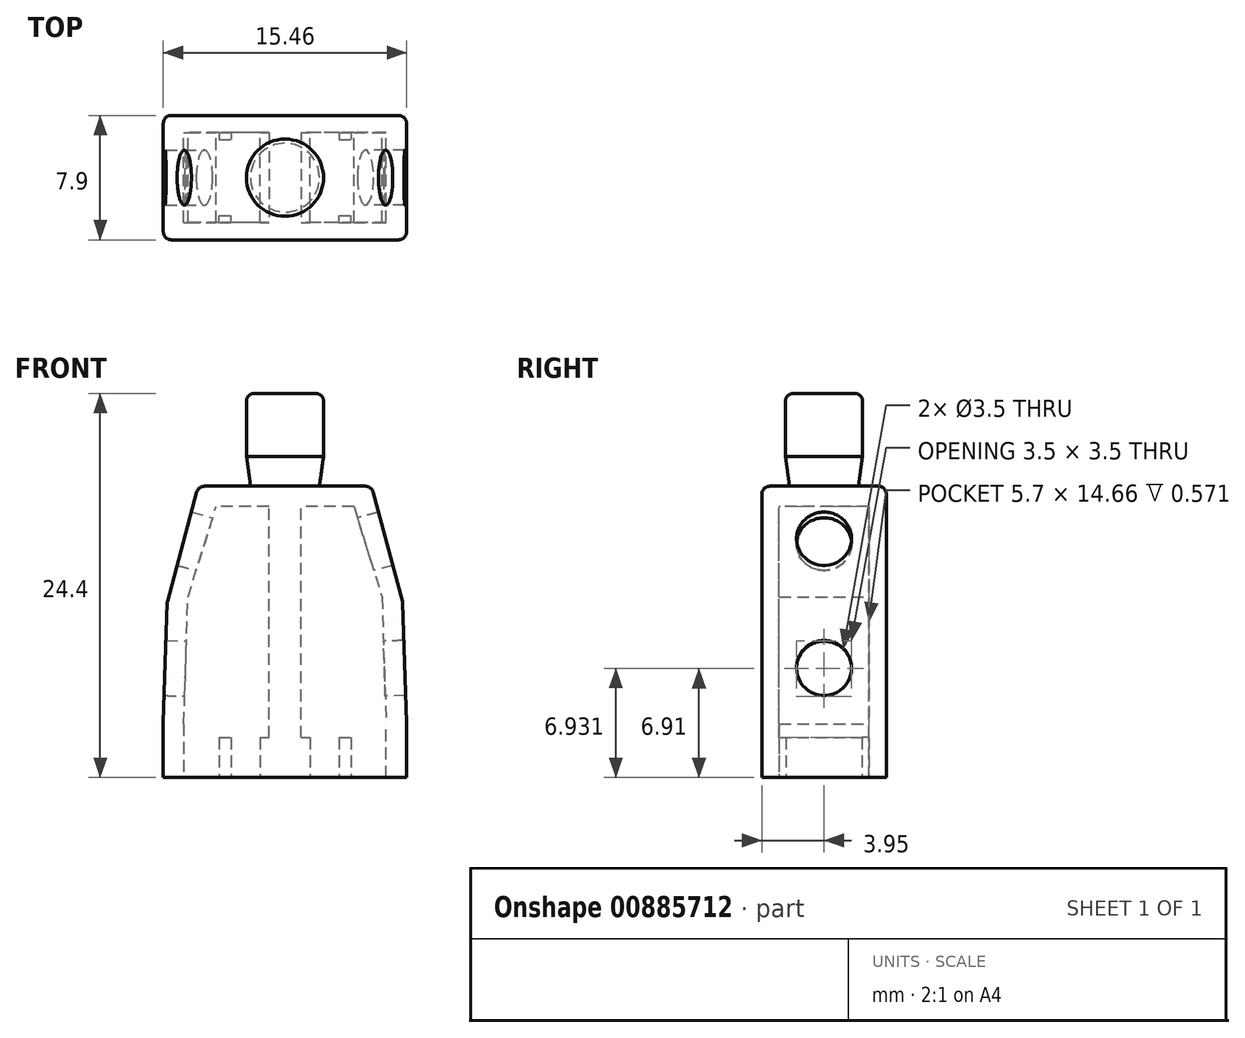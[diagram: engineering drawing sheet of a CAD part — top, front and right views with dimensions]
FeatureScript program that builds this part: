
annotation { "Feature Type Name" : "Feature", "Feature Type Description" : "" }
export const myFeature = defineFeature(function(context is Context, id is Id, definition is map)
    precondition{}
    {
        {
            var Q0;
            Q0=qCreatedBy(makeId("Front.planeOp"),FACE);
            var sketch = newSketch(context, id + "F0", { "sketchPlane" : qUnion([Q0])});
            skLineSegment(sketch, "E0", {"start": v(-7.72, 0) * mm, "end": v(-7.72, 3.5) * mm});
            skLineSegment(sketch, "E1", {"start": v(-7.72, 3.5) * mm, "end": v(-5.5, 18.5) * mm, "construction": true});
            skLineSegment(sketch, "E2", {"start": v(-5.5, 18.5) * mm, "end": v(5.5, 18.5) * mm});
            skLineSegment(sketch, "E3", {"start": v(5.5, 18.5) * mm, "end": v(7.73, 3.5) * mm, "construction": true});
            skLineSegment(sketch, "E4", {"start": v(7.73, 3.5) * mm, "end": v(7.73, 0) * mm});
            skLineSegment(sketch, "E5", {"start": v(7.72, 0) * mm, "end": v(6.43, 0) * mm});
            skLineSegment(sketch, "E6", {"start": v(6.42, 0) * mm, "end": v(6.42, 3.4) * mm});
            skLineSegment(sketch, "E7", {"start": v(6.43, 3.4) * mm, "end": v(4.38, 17.2) * mm, "construction": true});
            skLineSegment(sketch, "E8", {"start": v(4.38, 17.2) * mm, "end": v(-4.38, 17.2) * mm});
            skLineSegment(sketch, "E9", {"start": v(-4.38, 17.2) * mm, "end": v(-6.42, 3.4) * mm, "construction": true});
            skLineSegment(sketch, "E10", {"start": v(-6.42, 3.4) * mm, "end": v(-6.42, 0) * mm});
            skLineSegment(sketch, "E11", {"start": v(-6.43, 0) * mm, "end": v(-7.73, 0) * mm});
            skLineSegment(sketch, "E12", {"start": v(0, 0) * mm, "end": v(0, 17.2) * mm, "construction": true});
            skLineSegment(sketch, "E13", {"start": v(0, 17.2) * mm, "end": v(0, 18.5) * mm, "construction": true});
            skLineSegment(sketch, "E14", {"start": v(-6.61, 11) * mm, "end": v(-5.33, 10.8) * mm, "construction": true});
            skLineSegment(sketch, "E15", {"start": v(-5.5, 18.5) * mm, "end": v(-7.48, 11.13) * mm});
            skLineSegment(sketch, "E16", {"start": v(-7.48, 11.13) * mm, "end": v(-7.72, 3.5) * mm});
            skLineSegment(sketch, "E17", {"start": v(-6.42, 3.4) * mm, "end": v(-6.17, 11.45) * mm});
            skLineSegment(sketch, "E18", {"start": v(-6.17, 11.45) * mm, "end": v(-4.38, 17.2) * mm});
            skLineSegment(sketch, "E19", {"start": v(4.38, 17.2) * mm, "end": v(6.17, 11.45) * mm});
            skLineSegment(sketch, "E20", {"start": v(6.17, 11.45) * mm, "end": v(6.43, 3.4) * mm});
            skLineSegment(sketch, "E21", {"start": v(7.73, 3.5) * mm, "end": v(7.48, 11.13) * mm});
            skLineSegment(sketch, "E22", {"start": v(7.48, 11.13) * mm, "end": v(5.5, 18.5) * mm});
            skLineSegment(sketch, "E23", {"start": v(-5.27, 14.33) * mm, "end": v(-6.53, 14.66) * mm, "construction": true});
            skLineSegment(sketch, "E24", {"start": v(-6.3, 7.43) * mm, "end": v(-7.6, 7.47) * mm, "construction": true});
            skSolve(sketch);
        }
        {
            var Q0;
            Q0 = qSketchRegion(id + "F0", true);
            extrude(context, id + "F1", {"entities" : qUnion([Q0]), "depth" : 5.7 * mm, "offsetDistance" : 25.4 * mm, "symmetric" : true});
        }
        {
            var Q0;
            Q0=makeQuery(id+"F1.opExtrude","CAP_FACE",FACE,{"disambiguationData":[OSD([sQuery(id+"F0.wireOp",EDGE,"E0"),sQuery(id+"F0.wireOp",EDGE,"E1"),sQuery(id+"F0.wireOp",EDGE,"E2"),sQuery(id+"F0.wireOp",EDGE,"E3"),sQuery(id+"F0.wireOp",EDGE,"E4"),sQuery(id+"F0.wireOp",EDGE,"E5"),sQuery(id+"F0.wireOp",EDGE,"E6"),sQuery(id+"F0.wireOp",EDGE,"E7"),sQuery(id+"F0.wireOp",EDGE,"E8"),sQuery(id+"F0.wireOp",EDGE,"E9"),sQuery(id+"F0.wireOp",EDGE,"E10"),sQuery(id+"F0.wireOp",EDGE,"E11")])],"isStart":false});
            var sketch = newSketch(context, id + "F2", { "sketchPlane" : qUnion([Q0])});
            skLineSegment(sketch, "E25.0", {"start": v(-7.72, 0) * mm, "end": v(-7.72, 3.5) * mm});
            skLineSegment(sketch, "E25.1", {"start": v(-7.48, 11.13) * mm, "end": v(-7.72, 3.5) * mm});
            skLineSegment(sketch, "E25.2", {"start": v(-5.5, 18.5) * mm, "end": v(-7.48, 11.13) * mm});
            skLineSegment(sketch, "E25.3", {"start": v(-5.5, 18.5) * mm, "end": v(5.5, 18.5) * mm});
            skLineSegment(sketch, "E25.4", {"start": v(7.48, 11.13) * mm, "end": v(5.5, 18.5) * mm});
            skLineSegment(sketch, "E25.5", {"start": v(7.73, 3.5) * mm, "end": v(7.48, 11.13) * mm});
            skLineSegment(sketch, "E25.6", {"start": v(7.73, 3.5) * mm, "end": v(7.73, 0) * mm});
            skLineSegment(sketch, "E26", {"start": v(-7.73, 0) * mm, "end": v(7.73, 0) * mm});
            skSolve(sketch);
        }
        {
            var Q0;
            Q0 = qSketchRegion(id + "F2", true);
            extrude(context, id + "F3", {"entities" : qUnion([Q0]), "depth" : 1.1 * mm, "offsetDistance" : 25.4 * mm});
        }
        {
            var Q0;
            Q0=makeQuery(id+"F3.opExtrude","SWEPT_BODY",BODY,{"disambiguationData":[OSD([sQuery(id+"F2.wireOp",EDGE,"d7246907-a698-4353-8d18-1af56c573bea.0"),sQuery(id+"F2.wireOp",EDGE,"d7246907-a698-4353-8d18-1af56c573bea.1"),sQuery(id+"F2.wireOp",EDGE,"d7246907-a698-4353-8d18-1af56c573bea.2"),sQuery(id+"F2.wireOp",EDGE,"d7246907-a698-4353-8d18-1af56c573bea.3"),sQuery(id+"F2.wireOp",EDGE,"d7246907-a698-4353-8d18-1af56c573bea.4"),sQuery(id+"F2.wireOp",EDGE,"LrqN8bP0-91X3-xQIt-bfYl-7oQmGolxdx9D")])]});
            var Q1;
            Q1=makeQuery(id+"F3.opExtrude","SWEPT_BODY",BODY,{"disambiguationData":[OSD([sQuery(id+"F2.wireOp",EDGE,"E25.0"),sQuery(id+"F2.wireOp",EDGE,"E25.1"),sQuery(id+"F2.wireOp",EDGE,"E25.2"),sQuery(id+"F2.wireOp",EDGE,"E25.3"),sQuery(id+"F2.wireOp",EDGE,"E25.4"),sQuery(id+"F2.wireOp",EDGE,"E25.5"),sQuery(id+"F2.wireOp",EDGE,"E25.6"),sQuery(id+"F2.wireOp",EDGE,"E26")])]});
            var Q2;
            Q2=qCreatedBy(makeId("Front.planeOp"),FACE);
            mirror(context, id + "F4", {"operationType" : NewBodyOperationType.ADD, "entities" : qUnion([Q0, Q1]), "mirrorPlane" : qUnion([Q2])});
        }
        {
            var Q0;
            {var subQ0=makeQuery(id+"F3.opExtrude","SWEPT_FACE",FACE,{"disambiguationData":[OSD([sQuery(id+"F2.wireOp",EDGE,"d7246907-a698-4353-8d18-1af56c573bea.2")])]});Q0=makeQuery(id+"F4.boolean.opBoolean","MERGE",FACE,{"derivedFrom":[makeQuery(id+"F1.opExtrude","SWEPT_FACE",FACE,{"disambiguationData":[OSD([sQuery(id+"F0.wireOp",EDGE,"E2")])]}),subQ0,makeQuery(id+"F4.opPattern","COPY",FACE,{"derivedFrom":subQ0,"instanceName":"1"})]});}
            var sketch = newSketch(context, id + "F5", { "sketchPlane" : qUnion([Q0])});
            skCircle(sketch, "E27", {"center": v(0, 0) * mm, "radius": 2.45 * mm});
            skSolve(sketch);
        }
        {
            var Q0;
            Q0 = qSketchRegion(id + "F5", true);
            extrude(context, id + "F6", {"entities" : qUnion([Q0]), "operationType" : NewBodyOperationType.ADD, "depth" : 5.9 * mm, "offsetDistance" : 25.4 * mm});
        }
        {
            var Q0;
            {var subQ0=makeQuery(id+"F3.opExtrude","SWEPT_FACE",FACE,{"disambiguationData":[OSD([sQuery(id+"F2.wireOp",EDGE,"E25.2")])]});Q0=makeQuery(id+"F4.boolean.opBoolean","MERGE",FACE,{"derivedFrom":[makeQuery(id+"F1.opExtrude","SWEPT_FACE",FACE,{"disambiguationData":[OSD([sQuery(id+"F0.wireOp",EDGE,"E15")])]}),subQ0,makeQuery(id+"F4.opPattern","COPY",FACE,{"derivedFrom":subQ0,"instanceName":"1"})]});}
            var sketch = newSketch(context, id + "F7", { "sketchPlane" : qUnion([Q0])});
            skPoint(sketch, "E28", {"position": v(0, 13) * mm});
            skSolve(sketch);
        }
        {
            var Q0;
            {var subQ0=makeQuery(id+"F3.opExtrude","SWEPT_FACE",FACE,{"disambiguationData":[OSD([sQuery(id+"F2.wireOp",EDGE,"E25.4")])]});Q0=makeQuery(id+"F4.boolean.opBoolean","MERGE",FACE,{"derivedFrom":[makeQuery(id+"F1.opExtrude","SWEPT_FACE",FACE,{"disambiguationData":[OSD([sQuery(id+"F0.wireOp",EDGE,"E22")])]}),subQ0,makeQuery(id+"F4.opPattern","COPY",FACE,{"derivedFrom":subQ0,"instanceName":"1"})]});}
            var sketch = newSketch(context, id + "F8", { "sketchPlane" : qUnion([Q0])});
            skPoint(sketch, "E29", {"position": v(0, 13) * mm});
            skSolve(sketch);
        }
        {
            var Q0;
            {var subQ0=makeQuery(id+"F3.opExtrude","SWEPT_FACE",FACE,{"disambiguationData":[OSD([sQuery(id+"F2.wireOp",EDGE,"E25.1")])]});Q0=makeQuery(id+"F4.boolean.opBoolean","MERGE",FACE,{"derivedFrom":[makeQuery(id+"F1.opExtrude","SWEPT_FACE",FACE,{"disambiguationData":[OSD([sQuery(id+"F0.wireOp",EDGE,"E16")])]}),subQ0,makeQuery(id+"F4.opPattern","COPY",FACE,{"derivedFrom":subQ0,"instanceName":"1"})]});}
            var sketch = newSketch(context, id + "F9", { "sketchPlane" : qUnion([Q0])});
            skPoint(sketch, "E30", {"position": v(0, 6.7) * mm});
            skSolve(sketch);
        }
        {
            var Q0;
            {var subQ0=makeQuery(id+"F3.opExtrude","SWEPT_FACE",FACE,{"disambiguationData":[OSD([sQuery(id+"F2.wireOp",EDGE,"E25.5")])]});Q0=makeQuery(id+"F4.boolean.opBoolean","MERGE",FACE,{"derivedFrom":[makeQuery(id+"F1.opExtrude","SWEPT_FACE",FACE,{"disambiguationData":[OSD([sQuery(id+"F0.wireOp",EDGE,"E21")])]}),subQ0,makeQuery(id+"F4.opPattern","COPY",FACE,{"derivedFrom":subQ0,"instanceName":"1"})]});}
            var sketch = newSketch(context, id + "F10", { "sketchPlane" : qUnion([Q0])});
            skPoint(sketch, "E31", {"position": v(0, 6.7) * mm});
            skSolve(sketch);
        }
        {
            var Q0;
            Q0=sQuery(id+"F10.wireOp",VERTEX,"E31");
            var Q1;
            Q1=sQuery(id+"F8.wireOp",VERTEX,"E29");
            var Q2;
            Q2=sQuery(id+"F7.wireOp",VERTEX,"E28");
            var Q3;
            Q3=sQuery(id+"F9.wireOp",VERTEX,"E30");
            var Q4;
            Q4=makeQuery(id+"F1.opExtrude","SWEPT_BODY",BODY,{"disambiguationData":[OSD([sQuery(id+"F0.wireOp",EDGE,"E0"),sQuery(id+"F0.wireOp",EDGE,"E2"),sQuery(id+"F0.wireOp",EDGE,"E4"),sQuery(id+"F0.wireOp",EDGE,"E5"),sQuery(id+"F0.wireOp",EDGE,"E6"),sQuery(id+"F0.wireOp",EDGE,"E8"),sQuery(id+"F0.wireOp",EDGE,"E10"),sQuery(id+"F0.wireOp",EDGE,"E11"),sQuery(id+"F0.wireOp",EDGE,"E15"),sQuery(id+"F0.wireOp",EDGE,"E16"),sQuery(id+"F0.wireOp",EDGE,"E17"),sQuery(id+"F0.wireOp",EDGE,"E18"),sQuery(id+"F0.wireOp",EDGE,"E19"),sQuery(id+"F0.wireOp",EDGE,"E20"),sQuery(id+"F0.wireOp",EDGE,"E21"),sQuery(id+"F0.wireOp",EDGE,"E22")])]});
            hole(context, id + "F11", {"style" : HoleStyle.SIMPLE, "endStyle" : HoleEndStyle.BLIND, "holeDiameter" : 3.5 * mm, "majorDiameter" : 6.35 * mm, "holeDepth" : 2.54 * mm, "isTappedThrough" : true, "tappedDepth" : 12.7 * mm, "tapClearance" : 3, "locations" : qUnion([Q0, Q1, Q2, Q3]), "scope" : qUnion([Q4]), "startStyle" : HoleStartStyle.SKETCH});
        }
        {
            var Q0;
            Q0=makeQuery(id+"F1.opExtrude","SWEPT_FACE",FACE,{"disambiguationData":[OSD([sQuery(id+"F0.wireOp",EDGE,"E8")])]});
            var sketch = newSketch(context, id + "F12", { "sketchPlane" : qUnion([Q0])});
            skLineSegment(sketch, "E32.bottom", {"start": v(1.02, -2.85) * mm, "end": v(-1.02, -2.85) * mm});
            skLineSegment(sketch, "E32.top", {"start": v(1.02, 2.85) * mm, "end": v(-1.02, 2.85) * mm});
            skLineSegment(sketch, "E32.left", {"start": v(1.02, -2.85) * mm, "end": v(1.02, 2.85) * mm});
            skLineSegment(sketch, "E32.right", {"start": v(-1.02, -2.85) * mm, "end": v(-1.02, 2.85) * mm});
            skLineSegment(sketch, "E33", {"start": v(0, 0) * mm, "end": v(0, -2.85) * mm, "construction": true});
            skSolve(sketch);
        }
        {
            var Q0;
            Q0 = qSketchRegion(id + "F12", true);
            var Q1;
            {var subQ0=makeQuery(id+"F3.opExtrude","SWEPT_FACE",FACE,{"disambiguationData":[OSD([sQuery(id+"F2.wireOp",EDGE,"E26")])]});Q1=makeQuery(id+"F4.boolean.opBoolean","MERGE",FACE,{"derivedFrom":[makeQuery(id+"F1.opExtrude","SWEPT_FACE",FACE,{"disambiguationData":[OSD([sQuery(id+"F0.wireOp",EDGE,"E5")])]}),makeQuery(id+"F1.opExtrude","SWEPT_FACE",FACE,{"disambiguationData":[OSD([sQuery(id+"F0.wireOp",EDGE,"E11")])]}),subQ0,makeQuery(id+"F4.opPattern","COPY",FACE,{"derivedFrom":subQ0,"instanceName":"1"})]});}
            extrude(context, id + "F13", {"entities" : qUnion([Q0]), "operationType" : NewBodyOperationType.ADD, "endBound" : BoundingType.UP_TO_SURFACE, "depth" : 25.4 * mm, "endBoundEntityFace" : qUnion([Q1]), "offsetDistance" : 25.4 * mm});
        }
        {
            var Q0;
            Q0=makeQuery(id+"F4.opPattern","COPY",EDGE,{"derivedFrom":makeQuery(id+"F3.opExtrude","CAP_EDGE",EDGE,{"disambiguationData":[OSD([sQuery(id+"F2.wireOp",EDGE,"E25.6")])],"isStart":false}),"instanceName":"1"});
            var Q1;
            Q1=makeQuery(id+"F4.opPattern","COPY",EDGE,{"derivedFrom":makeQuery(id+"F3.opExtrude","CAP_EDGE",EDGE,{"disambiguationData":[OSD([sQuery(id+"F2.wireOp",EDGE,"E25.5")])],"isStart":false}),"instanceName":"1"});
            var Q2;
            Q2=makeQuery(id+"F4.opPattern","COPY",EDGE,{"derivedFrom":makeQuery(id+"F3.opExtrude","CAP_EDGE",EDGE,{"disambiguationData":[OSD([sQuery(id+"F2.wireOp",EDGE,"E25.4")])],"isStart":false}),"instanceName":"1"});
            var Q3;
            Q3=makeQuery(id+"F4.opPattern","COPY",EDGE,{"derivedFrom":makeQuery(id+"F3.opExtrude","CAP_EDGE",EDGE,{"disambiguationData":[OSD([sQuery(id+"F2.wireOp",EDGE,"E25.3")])],"isStart":false}),"instanceName":"1"});
            var Q4;
            Q4=makeQuery(id+"F4.opPattern","COPY",EDGE,{"derivedFrom":makeQuery(id+"F3.opExtrude","CAP_EDGE",EDGE,{"disambiguationData":[OSD([sQuery(id+"F2.wireOp",EDGE,"E25.2")])],"isStart":false}),"instanceName":"1"});
            var Q5;
            Q5=makeQuery(id+"F4.opPattern","COPY",EDGE,{"derivedFrom":makeQuery(id+"F3.opExtrude","CAP_EDGE",EDGE,{"disambiguationData":[OSD([sQuery(id+"F2.wireOp",EDGE,"E25.0")])],"isStart":false}),"instanceName":"1"});
            var Q6;
            Q6=makeQuery(id+"F4.opPattern","COPY",EDGE,{"derivedFrom":makeQuery(id+"F3.opExtrude","CAP_EDGE",EDGE,{"disambiguationData":[OSD([sQuery(id+"F2.wireOp",EDGE,"E25.1")])],"isStart":false}),"instanceName":"1"});
            var Q7;
            Q7=makeQuery(id+"F3.opExtrude","CAP_EDGE",EDGE,{"disambiguationData":[OSD([sQuery(id+"F2.wireOp",EDGE,"E25.0")])],"isStart":false});
            var Q8;
            Q8=makeQuery(id+"F3.opExtrude","CAP_EDGE",EDGE,{"disambiguationData":[OSD([sQuery(id+"F2.wireOp",EDGE,"E25.1")])],"isStart":false});
            var Q9;
            Q9=makeQuery(id+"F3.opExtrude","CAP_EDGE",EDGE,{"disambiguationData":[OSD([sQuery(id+"F2.wireOp",EDGE,"E25.2")])],"isStart":false});
            var Q10;
            Q10=makeQuery(id+"F3.opExtrude","CAP_EDGE",EDGE,{"disambiguationData":[OSD([sQuery(id+"F2.wireOp",EDGE,"E25.3")])],"isStart":false});
            var Q11;
            {var subQ0=makeQuery(id+"F3.opExtrude","SWEPT_EDGE",EDGE,{"disambiguationData":[OSD([sQuery(id+"F2.wireOp",EDGE,"E25.2"),sQuery(id+"F2.wireOp",EDGE,"E25.3")])]});Q11=makeQuery(id+"F4.boolean.opBoolean","MERGE",EDGE,{"derivedFrom":[makeQuery(id+"F1.opExtrude","SWEPT_EDGE",EDGE,{"disambiguationData":[OSD([sQuery(id+"F0.wireOp",EDGE,"E2"),sQuery(id+"F0.wireOp",EDGE,"E15")])]}),subQ0,makeQuery(id+"F4.opPattern","COPY",EDGE,{"derivedFrom":subQ0,"instanceName":"1"})]});}
            var Q12;
            Q12=makeQuery(id+"F3.opExtrude","CAP_EDGE",EDGE,{"disambiguationData":[OSD([sQuery(id+"F2.wireOp",EDGE,"E25.6")])],"isStart":false});
            var Q13;
            Q13=makeQuery(id+"F3.opExtrude","CAP_EDGE",EDGE,{"disambiguationData":[OSD([sQuery(id+"F2.wireOp",EDGE,"E25.5")])],"isStart":false});
            var Q14;
            Q14=makeQuery(id+"F3.opExtrude","CAP_EDGE",EDGE,{"disambiguationData":[OSD([sQuery(id+"F2.wireOp",EDGE,"E25.4")])],"isStart":false});
            var Q15;
            {var subQ0=makeQuery(id+"F3.opExtrude","SWEPT_EDGE",EDGE,{"disambiguationData":[OSD([sQuery(id+"F2.wireOp",EDGE,"E25.3"),sQuery(id+"F2.wireOp",EDGE,"E25.4")])]});Q15=makeQuery(id+"F4.boolean.opBoolean","MERGE",EDGE,{"derivedFrom":[makeQuery(id+"F1.opExtrude","SWEPT_EDGE",EDGE,{"disambiguationData":[OSD([sQuery(id+"F0.wireOp",EDGE,"E2"),sQuery(id+"F0.wireOp",EDGE,"E22")])]}),subQ0,makeQuery(id+"F4.opPattern","COPY",EDGE,{"derivedFrom":subQ0,"instanceName":"1"})]});}
            var Q16;
            {var subQ0=makeQuery(id+"F3.opExtrude","SWEPT_EDGE",EDGE,{"disambiguationData":[OSD([sQuery(id+"F2.wireOp",EDGE,"E25.4"),sQuery(id+"F2.wireOp",EDGE,"E25.5")])]});Q16=makeQuery(id+"F4.boolean.opBoolean","MERGE",EDGE,{"derivedFrom":[makeQuery(id+"F1.opExtrude","SWEPT_EDGE",EDGE,{"disambiguationData":[OSD([sQuery(id+"F0.wireOp",EDGE,"E21"),sQuery(id+"F0.wireOp",EDGE,"E22")])]}),subQ0,makeQuery(id+"F4.opPattern","COPY",EDGE,{"derivedFrom":subQ0,"instanceName":"1"})]});}
            var Q17;
            {var subQ0=makeQuery(id+"F3.opExtrude","SWEPT_EDGE",EDGE,{"disambiguationData":[OSD([sQuery(id+"F2.wireOp",EDGE,"E25.5"),sQuery(id+"F2.wireOp",EDGE,"E25.6")])]});Q17=makeQuery(id+"F4.boolean.opBoolean","MERGE",EDGE,{"derivedFrom":[makeQuery(id+"F1.opExtrude","SWEPT_EDGE",EDGE,{"disambiguationData":[OSD([sQuery(id+"F0.wireOp",EDGE,"E4"),sQuery(id+"F0.wireOp",EDGE,"E21")])]}),subQ0,makeQuery(id+"F4.opPattern","COPY",EDGE,{"derivedFrom":subQ0,"instanceName":"1"})]});}
            var Q18;
            {var subQ0=makeQuery(id+"F3.opExtrude","SWEPT_EDGE",EDGE,{"disambiguationData":[OSD([sQuery(id+"F2.wireOp",EDGE,"E25.0"),sQuery(id+"F2.wireOp",EDGE,"E25.1")])]});Q18=makeQuery(id+"F4.boolean.opBoolean","MERGE",EDGE,{"derivedFrom":[makeQuery(id+"F1.opExtrude","SWEPT_EDGE",EDGE,{"disambiguationData":[OSD([sQuery(id+"F0.wireOp",EDGE,"E0"),sQuery(id+"F0.wireOp",EDGE,"E16")])]}),subQ0,makeQuery(id+"F4.opPattern","COPY",EDGE,{"derivedFrom":subQ0,"instanceName":"1"})]});}
            var Q19;
            {var subQ0=makeQuery(id+"F3.opExtrude","SWEPT_EDGE",EDGE,{"disambiguationData":[OSD([sQuery(id+"F2.wireOp",EDGE,"E25.1"),sQuery(id+"F2.wireOp",EDGE,"E25.2")])]});Q19=makeQuery(id+"F4.boolean.opBoolean","MERGE",EDGE,{"derivedFrom":[makeQuery(id+"F1.opExtrude","SWEPT_EDGE",EDGE,{"disambiguationData":[OSD([sQuery(id+"F0.wireOp",EDGE,"E15"),sQuery(id+"F0.wireOp",EDGE,"E16")])]}),subQ0,makeQuery(id+"F4.opPattern","COPY",EDGE,{"derivedFrom":subQ0,"instanceName":"1"})]});}
            var Q20;
            Q20=makeQuery(id+"F6.opExtrude","CAP_EDGE",EDGE,{"disambiguationData":[OSD([sQuery(id+"F5.wireOp",EDGE,"E27")])],"isStart":false});
            fillet(context, id + "F14", {"entities" : qUnion([Q0, Q1, Q2, Q3, Q4, Q5, Q6, Q7, Q8, Q9, Q10, Q11, Q12, Q13, Q14, Q15, Q16, Q17, Q18, Q19, Q20]), "radius" : 0.5 * mm, "tangentPropagation" : true, "allowEdgeOverflow" : false});
        }
        {
            var Q0;
            Q0=qCreatedBy(makeId("Top.planeOp"),FACE);
            var sketch = newSketch(context, id + "F15", { "sketchPlane" : qUnion([Q0])});
            skLineSegment(sketch, "E34.bottom", {"start": v(-1.59, -2.85) * mm, "end": v(1.59, -2.85) * mm});
            skLineSegment(sketch, "E34.top", {"start": v(-1.59, 2.85) * mm, "end": v(1.59, 2.85) * mm});
            skLineSegment(sketch, "E34.left", {"start": v(-1.59, -2.85) * mm, "end": v(-1.59, 2.85) * mm});
            skLineSegment(sketch, "E34.right", {"start": v(1.59, -2.85) * mm, "end": v(1.59, 2.85) * mm});
            skLineSegment(sketch, "E35", {"start": v(0, 0) * mm, "end": v(0, 2.85) * mm, "construction": true});
            skLineSegment(sketch, "E36.bottom", {"start": v(3.43, -2.85) * mm, "end": v(4.2, -2.85) * mm});
            skLineSegment(sketch, "E36.top", {"start": v(3.43, -2.41) * mm, "end": v(4.2, -2.41) * mm});
            skLineSegment(sketch, "E36.left", {"start": v(3.43, -2.85) * mm, "end": v(3.43, -2.41) * mm});
            skLineSegment(sketch, "E36.right", {"start": v(4.2, -2.85) * mm, "end": v(4.2, -2.41) * mm});
            skLineSegment(sketch, "E37.bottom", {"start": v(3.43, 2.85) * mm, "end": v(4.2, 2.85) * mm});
            skLineSegment(sketch, "E37.top", {"start": v(3.43, 2.41) * mm, "end": v(4.2, 2.41) * mm});
            skLineSegment(sketch, "E37.left", {"start": v(3.43, 2.85) * mm, "end": v(3.43, 2.41) * mm});
            skLineSegment(sketch, "E37.right", {"start": v(4.2, 2.85) * mm, "end": v(4.2, 2.41) * mm});
            skLineSegment(sketch, "E38.bottom", {"start": v(-4.2, 2.85) * mm, "end": v(-3.43, 2.85) * mm});
            skLineSegment(sketch, "E38.top", {"start": v(-4.2, 2.41) * mm, "end": v(-3.43, 2.41) * mm});
            skLineSegment(sketch, "E38.left", {"start": v(-4.2, 2.85) * mm, "end": v(-4.2, 2.41) * mm});
            skLineSegment(sketch, "E38.right", {"start": v(-3.43, 2.85) * mm, "end": v(-3.43, 2.41) * mm});
            skLineSegment(sketch, "E39.bottom", {"start": v(-4.2, -2.85) * mm, "end": v(-3.43, -2.85) * mm});
            skLineSegment(sketch, "E39.top", {"start": v(-4.2, -2.41) * mm, "end": v(-3.43, -2.41) * mm});
            skLineSegment(sketch, "E39.left", {"start": v(-4.2, -2.85) * mm, "end": v(-4.2, -2.41) * mm});
            skLineSegment(sketch, "E39.right", {"start": v(-3.43, -2.85) * mm, "end": v(-3.43, -2.41) * mm});
            skLineSegment(sketch, "E40", {"start": v(-3.81, 2.85) * mm, "end": v(3.81, 2.85) * mm, "construction": true});
            skSolve(sketch);
        }
        {
            var Q0;
            Q0 = qSketchRegion(id + "F15", true);
            extrude(context, id + "F16", {"entities" : qUnion([Q0]), "operationType" : NewBodyOperationType.ADD, "depth" : 2.54 * mm, "offsetDistance" : 25.4 * mm});
        }
        {
            var Q0;
            {var subQ0=makeQuery(id+"F3.opExtrude","SWEPT_FACE",FACE,{"disambiguationData":[OSD([sQuery(id+"F2.wireOp",EDGE,"E25.3")])]});Q0=makeQuery(id+"F4.boolean.opBoolean","MERGE",FACE,{"derivedFrom":[makeQuery(id+"F1.opExtrude","SWEPT_FACE",FACE,{"disambiguationData":[OSD([sQuery(id+"F0.wireOp",EDGE,"E2")])]}),subQ0,makeQuery(id+"F4.opPattern","COPY",FACE,{"derivedFrom":subQ0,"instanceName":"1"})]});}
            var sketch = newSketch(context, id + "F17", { "sketchPlane" : qUnion([Q0])});
            skCircle(sketch, "E41", {"center": v(0, 0) * mm, "radius": 2.18 * mm});
            skCircle(sketch, "E42", {"center": v(0, 0) * mm, "radius": 3.18 * mm});
            skSolve(sketch);
        }
        {
            var Q0;
            Q0 = qSketchRegion(id + "F17", true);
            extrude(context, id + "F18", {"entities" : qUnion([Q0]), "operationType" : NewBodyOperationType.REMOVE, "depth" : 5.08 * mm, "offsetDistance" : 25.4 * mm, "hasDraft" : true, "draftAngle" : 8 * degree, "draftPullDirection" : true});
        }
    });
